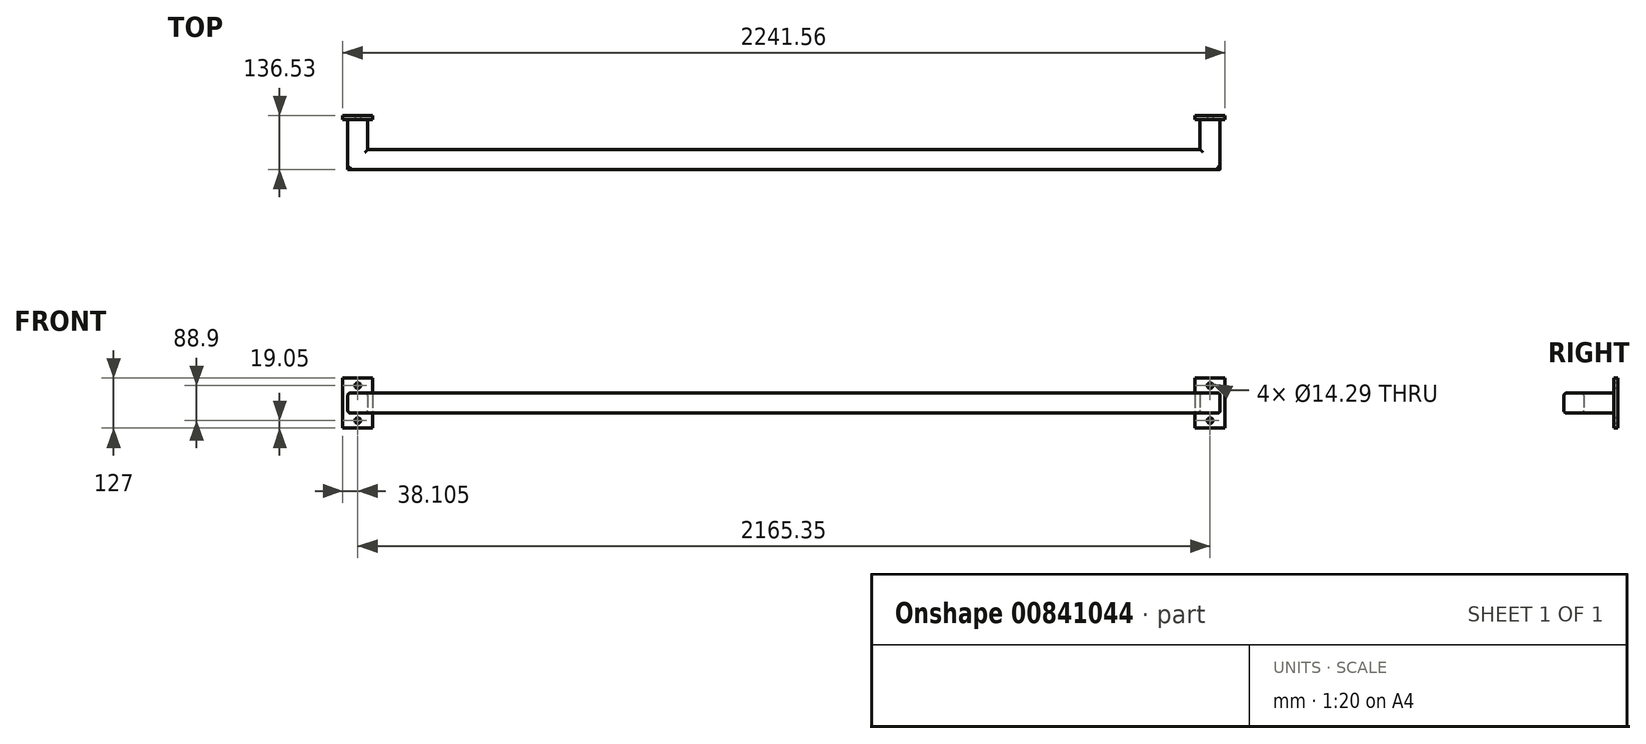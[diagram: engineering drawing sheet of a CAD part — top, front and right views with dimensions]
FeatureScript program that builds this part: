
annotation { "Feature Type Name" : "Feature", "Feature Type Description" : "" }
export const myFeature = defineFeature(function(context is Context, id is Id, definition is map)
    precondition{}
    {
        {
            var Q0;
            Q0=qCreatedBy(makeId("Front.planeOp"),FACE);
            var sketch = newSketch(context, id + "F0", { "sketchPlane" : qUnion([Q0])});
            skLineSegment(sketch, "E0", {"start": v(0, 665.57) * mm, "end": v(0, -639.63) * mm, "construction": true});
            skLineSegment(sketch, "E1", {"start": v(-1082.67, 0) * mm, "end": v(1082.67, 0) * mm, "construction": true});
            skLineSegment(sketch, "E2.bottom", {"start": v(-1101.72, 25.4) * mm, "end": v(-1063.62, 25.4) * mm});
            skLineSegment(sketch, "E2.top", {"start": v(-1101.72, -25.4) * mm, "end": v(-1063.62, -25.4) * mm});
            skLineSegment(sketch, "E2.left", {"start": v(-1108.07, 19.05) * mm, "end": v(-1108.07, -19.05) * mm});
            skLineSegment(sketch, "E2.right", {"start": v(-1057.27, 19.05) * mm, "end": v(-1057.27, -19.05) * mm});
            skPoint(sketch, "E2.middle", {"position": v(-1082.67, 0) * mm});
            skPoint(sketch, "E3.visualSharp", {"position": v(-1108.07, 25.4) * mm});
            skArc(sketch, "E3.filletArc", {"start": v(-1101.72, 25.4) * mm, "mid": v(-1106.22, 23.54) * mm, "end": v(-1108.07, 19.05) * mm});
            skPoint(sketch, "E4.visualSharp", {"position": v(-1057.27, 25.4) * mm});
            skArc(sketch, "E4.filletArc", {"start": v(-1057.27, 19.05) * mm, "mid": v(-1059.13, 23.54) * mm, "end": v(-1063.62, 25.4) * mm});
            skPoint(sketch, "E5.visualSharp", {"position": v(-1057.27, -25.4) * mm});
            skArc(sketch, "E5.filletArc", {"start": v(-1063.62, -25.4) * mm, "mid": v(-1059.13, -23.54) * mm, "end": v(-1057.27, -19.05) * mm});
            skPoint(sketch, "E6.visualSharp", {"position": v(-1108.07, -25.4) * mm});
            skArc(sketch, "E6.filletArc", {"start": v(-1108.07, -19.05) * mm, "mid": v(-1106.22, -23.54) * mm, "end": v(-1101.72, -25.4) * mm});
            skLineSegment(sketch, "E7.bottom", {"start": v(-1120.78, 63.5) * mm, "end": v(-1044.58, 63.5) * mm});
            skLineSegment(sketch, "E7.top", {"start": v(-1120.78, -63.5) * mm, "end": v(-1044.58, -63.5) * mm});
            skLineSegment(sketch, "E7.left", {"start": v(-1120.78, 63.5) * mm, "end": v(-1120.78, -63.5) * mm});
            skLineSegment(sketch, "E7.right", {"start": v(-1044.58, 63.5) * mm, "end": v(-1044.58, -63.5) * mm});
            skSolve(sketch);
        }
        {
            var Q0;
            Q0=makeQuery(id+"F0.imprint","IMPRINT",FACE,{"disambiguationData":[TD([[makeQuery(id+"F0.imprint","IMPRINT",EDGE,{"derivedFrom":sQuery(id+"F0.wireOp",EDGE,"E2.bottom")}),1.0]])]});
            var Q1;
            Q1=makeQuery(id+"F0.imprint","IMPRINT",FACE,{"disambiguationData":[TD([[makeQuery(id+"F0.imprint","IMPRINT",EDGE,{"derivedFrom":sQuery(id+"F0.wireOp",EDGE,"E2.bottom")}),-1.0]])]});
            extrude(context, id + "F1", {"entities" : qUnion([Q0, Q1]), "depth" : 9.52 * mm, "offsetDistance" : 25.4 * mm});
        }
        {
            var Q0;
            Q0=makeQuery(id+"F1.opExtrude","CAP_FACE",FACE,{"disambiguationData":[OSD([sQuery(id+"F0.wireOp",EDGE,"E7.bottom"),sQuery(id+"F0.wireOp",EDGE,"E7.top"),sQuery(id+"F0.wireOp",EDGE,"E7.left"),sQuery(id+"F0.wireOp",EDGE,"E7.right")])],"isStart":false});
            var sketch = newSketch(context, id + "F2", { "sketchPlane" : qUnion([Q0])});
            skLineSegment(sketch, "E8.0", {"start": v(-1101.72, 25.4) * mm, "end": v(-1063.62, 25.4) * mm, "construction": true});
            skLineSegment(sketch, "E9.0", {"start": v(-1082.67, 0) * mm, "end": v(1082.67, 0) * mm, "construction": true});
            skLineSegment(sketch, "E10", {"start": v(-1082.67, 25.4) * mm, "end": v(-1082.67, 63.5) * mm, "construction": true});
            skCircle(sketch, "E11", {"center": v(-1082.67, 44.45) * mm, "radius": 7.14 * mm});
            skCircle(sketch, "E12.MirrorC", {"center": v(-1082.67, -44.45) * mm, "radius": 7.14 * mm});
            skSolve(sketch);
        }
        {
            var Q0;
            Q0 = qSketchRegion(id + "F2", true);
            extrude(context, id + "F3", {"entities" : qUnion([Q0]), "operationType" : NewBodyOperationType.REMOVE, "oppositeDirection" : true, "depth" : 25.4 * mm, "offsetDistance" : 25.4 * mm});
        }
        {
            var Q0;
            Q0=makeQuery(id+"F1.opExtrude","SWEPT_BODY",BODY,{"disambiguationData":[OSD([sQuery(id+"F0.wireOp",EDGE,"E7.bottom"),sQuery(id+"F0.wireOp",EDGE,"E7.top"),sQuery(id+"F0.wireOp",EDGE,"E7.left"),sQuery(id+"F0.wireOp",EDGE,"E7.right")])]});
            var Q1;
            Q1=qCreatedBy(makeId("Right.planeOp"),FACE);
            mirror(context, id + "F4", {"entities" : qUnion([Q0]), "mirrorPlane" : qUnion([Q1])});
        }
        {
            var Q0;
            Q0=makeQuery(id+"F1.opExtrude","CAP_FACE",FACE,{"disambiguationData":[OSD([sQuery(id+"F0.wireOp",EDGE,"E7.bottom"),sQuery(id+"F0.wireOp",EDGE,"E7.top"),sQuery(id+"F0.wireOp",EDGE,"E7.left"),sQuery(id+"F0.wireOp",EDGE,"E7.right")])],"isStart":false});
            var sketch = newSketch(context, id + "F5", { "sketchPlane" : qUnion([Q0])});
            skLineSegment(sketch, "E13.0", {"start": v(-1101.72, 25.4) * mm, "end": v(-1063.62, 25.4) * mm});
            skArc(sketch, "E14.0", {"start": v(-1057.27, 19.05) * mm, "mid": v(-1059.13, 23.54) * mm, "end": v(-1063.62, 25.4) * mm});
            skLineSegment(sketch, "E15.0", {"start": v(-1057.27, 19.05) * mm, "end": v(-1057.27, -19.05) * mm});
            skArc(sketch, "E16.0", {"start": v(-1063.62, -25.4) * mm, "mid": v(-1059.13, -23.54) * mm, "end": v(-1057.27, -19.05) * mm});
            skLineSegment(sketch, "E17.0", {"start": v(-1101.72, -25.4) * mm, "end": v(-1063.62, -25.4) * mm});
            skPoint(sketch, "E18.0", {"position": v(-1106.22, -23.54) * mm});
            skArc(sketch, "E19.0", {"start": v(-1108.07, -19.05) * mm, "mid": v(-1106.22, -23.54) * mm, "end": v(-1101.72, -25.4) * mm});
            skLineSegment(sketch, "E20.0", {"start": v(-1108.07, 19.05) * mm, "end": v(-1108.07, -19.05) * mm});
            skArc(sketch, "E21.0", {"start": v(-1101.72, 25.4) * mm, "mid": v(-1106.22, 23.54) * mm, "end": v(-1108.07, 19.05) * mm});
            skSolve(sketch);
        }
        {
            var Q0;
            Q0=qCreatedBy(makeId("Top.planeOp"),FACE);
            var sketch = newSketch(context, id + "F6", { "sketchPlane" : qUnion([Q0])});
            skPoint(sketch, "E22.0", {"position": v(-1082.67, 0) * mm});
            skPoint(sketch, "E23.0", {"position": v(1082.67, -9.53) * mm});
            skPoint(sketch, "E24.0", {"position": v(-1082.67, -9.53) * mm});
            skLineSegment(sketch, "E25", {"start": v(-1082.67, -9.52) * mm, "end": v(-1082.67, -111.12) * mm});
            skLineSegment(sketch, "E26", {"start": v(-1082.67, -111.12) * mm, "end": v(1082.67, -111.12) * mm});
            skLineSegment(sketch, "E27", {"start": v(1082.67, -111.12) * mm, "end": v(1082.67, -9.52) * mm});
            skSolve(sketch);
        }
        {
            var Q0;
            Q0=makeQuery(id+"F5.imprint","IMPRINT",FACE,{"disambiguationData":[TD([[makeQuery(id+"F5.imprint","IMPRINT",EDGE,{"derivedFrom":sQuery(id+"F5.wireOp",EDGE,"E13.0")}),-1.0]])]});
            var Q1;
            Q1=sQuery(id+"F6.wireOp",EDGE,"E25");
            var Q2;
            Q2=sQuery(id+"F6.wireOp",EDGE,"E26");
            var Q3;
            Q3=sQuery(id+"F6.wireOp",EDGE,"E27");
            sweep(context, id + "F7", {"profiles" : qUnion([Q0]), "path" : qUnion([Q1, Q2, Q3])});
        }
    });
